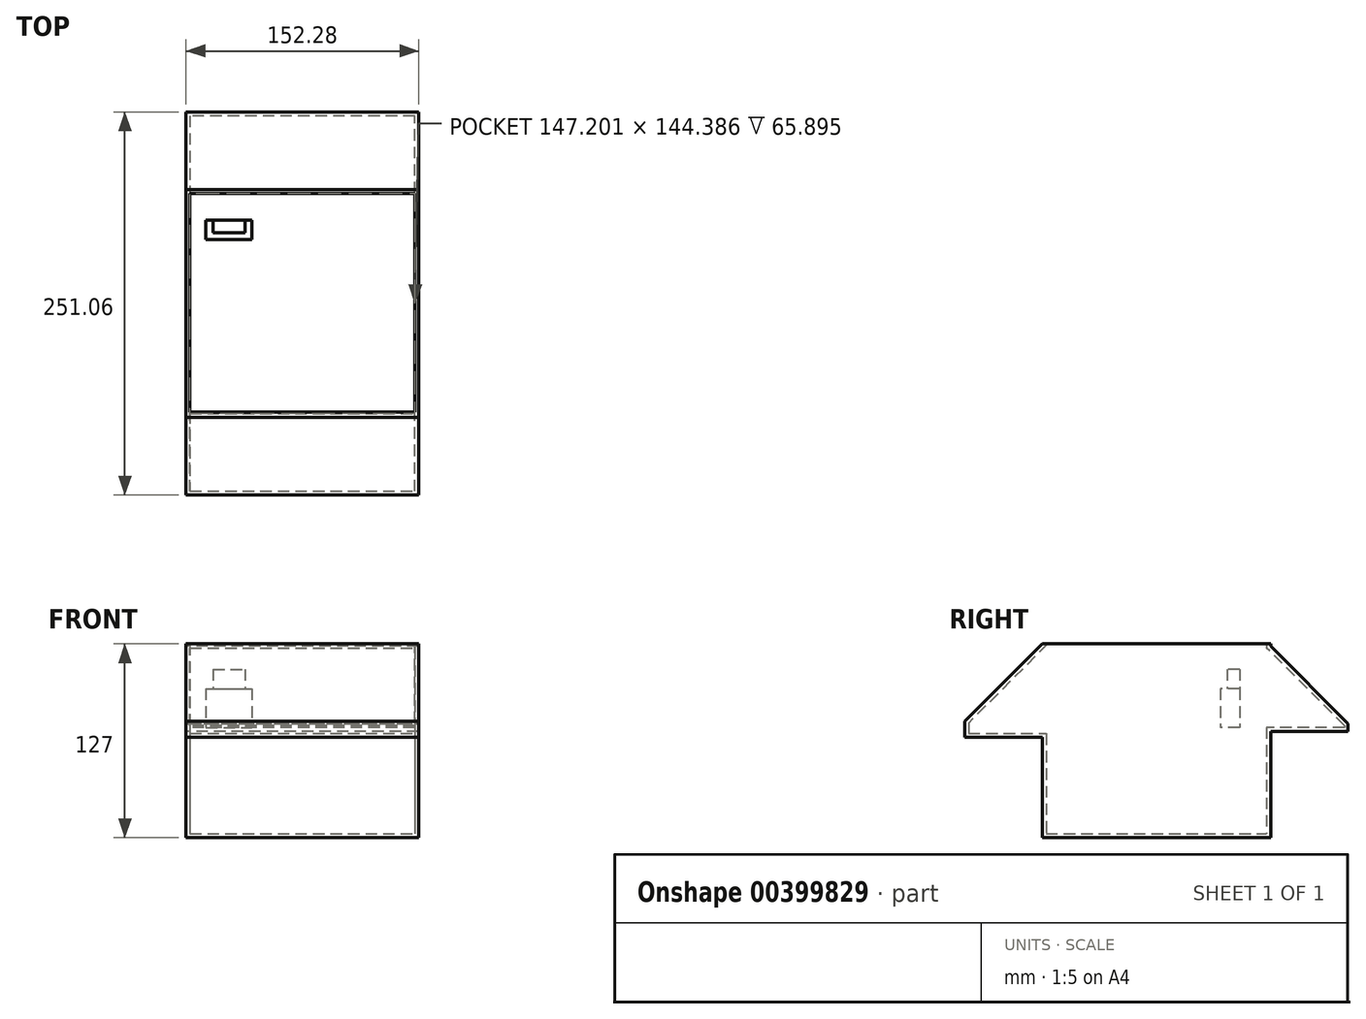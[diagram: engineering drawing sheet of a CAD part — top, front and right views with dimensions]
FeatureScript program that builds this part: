
annotation { "Feature Type Name" : "Feature", "Feature Type Description" : "" }
export const myFeature = defineFeature(function(context is Context, id is Id, definition is map)
    precondition{}
    {
        {
            var Q0;
            Q0=qCreatedBy(makeId("Top.planeOp"),FACE);
            var sketch = newSketch(context, id + "F0", { "sketchPlane" : qUnion([Q0])});
            skLineSegment(sketch, "E0.bottom", {"start": v(-76.8, -74.45) * mm, "end": v(75.48, -74.45) * mm});
            skLineSegment(sketch, "E0.top", {"start": v(-76.8, 75.01) * mm, "end": v(75.48, 75.01) * mm});
            skLineSegment(sketch, "E0.left", {"start": v(-76.8, -74.45) * mm, "end": v(-76.8, 75.01) * mm});
            skLineSegment(sketch, "E0.right", {"start": v(75.48, -74.45) * mm, "end": v(75.48, 75.01) * mm});
            skSolve(sketch);
        }
        {
            var Q0;
            Q0=makeQuery(id+"F0.imprint","IMPRINT",FACE,{"disambiguationData":[TD([[makeQuery(id+"F0.imprint","IMPRINT",EDGE,{"derivedFrom":sQuery(id+"F0.wireOp",EDGE,"E0.bottom")}),1.0]])]});
            extrude(context, id + "F1", {"entities" : qUnion([Q0]), "depth" : 127 * mm});
        }
        {
            var Q0;
            Q0=makeQuery(id+"F1.opExtrude","SWEPT_FACE",FACE,{"disambiguationData":[OSD([sQuery(id+"F0.wireOp",EDGE,"E0.bottom")])]});
            var sketch = newSketch(context, id + "F2", { "sketchPlane" : qUnion([Q0])});
            skLineSegment(sketch, "E1.bottom", {"start": v(-76.8, 127) * mm, "end": v(75.48, 127) * mm});
            skLineSegment(sketch, "E1.top", {"start": v(-76.8, 65.9) * mm, "end": v(75.48, 65.9) * mm});
            skLineSegment(sketch, "E1.left", {"start": v(-76.8, 127) * mm, "end": v(-76.8, 65.9) * mm});
            skLineSegment(sketch, "E1.right", {"start": v(75.48, 127) * mm, "end": v(75.48, 65.9) * mm});
            skSolve(sketch);
        }
        {
            var Q0;
            Q0=makeQuery(id+"F2.imprint","IMPRINT",FACE,{"disambiguationData":[TD([[makeQuery(id+"F2.imprint","IMPRINT",EDGE,{"derivedFrom":sQuery(id+"F2.wireOp",EDGE,"E1.bottom")}),-1.0]])]});
            extrude(context, id + "F3", {"entities" : qUnion([Q0]), "operationType" : NewBodyOperationType.ADD, "depth" : 50.8 * mm});
        }
        {
            var Q0;
            Q0=makeQuery(id+"F1.opExtrude","SWEPT_FACE",FACE,{"disambiguationData":[OSD([sQuery(id+"F0.wireOp",EDGE,"E0.top")])]});
            var sketch = newSketch(context, id + "F4", { "sketchPlane" : qUnion([Q0])});
            skLineSegment(sketch, "E2.bottom", {"start": v(-75.48, 125.47) * mm, "end": v(76.8, 125.47) * mm});
            skLineSegment(sketch, "E2.top", {"start": v(-75.48, 69.75) * mm, "end": v(76.8, 69.75) * mm});
            skLineSegment(sketch, "E2.left", {"start": v(-75.48, 125.47) * mm, "end": v(-75.48, 69.75) * mm});
            skLineSegment(sketch, "E2.right", {"start": v(76.8, 125.47) * mm, "end": v(76.8, 69.75) * mm});
            skSolve(sketch);
        }
        {
            var Q0;
            Q0=makeQuery(id+"F4.imprint","IMPRINT",FACE,{"disambiguationData":[TD([[makeQuery(id+"F4.imprint","IMPRINT",EDGE,{"derivedFrom":sQuery(id+"F4.wireOp",EDGE,"E2.bottom")}),-1.0]])]});
            extrude(context, id + "F5", {"entities" : qUnion([Q0]), "operationType" : NewBodyOperationType.ADD, "depth" : 50.8 * mm});
        }
        {
            var Q0;
            Q0=makeQuery(id+"F5.opExtrude","CAP_EDGE",EDGE,{"disambiguationData":[OSD([sQuery(id+"F4.wireOp",EDGE,"E2.bottom")])],"isStart":false});
            chamfer(context, id + "F6", {"entities" : qUnion([Q0]), "width" : 50.8 * mm, "tangentPropagation" : true});
        }
        {
            var Q0;
            Q0=makeQuery(id+"F3.opExtrude","CAP_EDGE",EDGE,{"disambiguationData":[OSD([sQuery(id+"F2.wireOp",EDGE,"E1.bottom")])],"isStart":false});
            chamfer(context, id + "F7", {"entities" : qUnion([Q0]), "width" : 50.8 * mm, "tangentPropagation" : true});
        }
        {
            var Q0;
            Q0=makeQuery(id+"F3.boolean.opBoolean","MERGE",FACE,{"derivedFrom":[makeQuery(id+"F1.opExtrude","CAP_FACE",FACE,{"disambiguationData":[OSD([sQuery(id+"F0.wireOp",EDGE,"E0.bottom"),sQuery(id+"F0.wireOp",EDGE,"E0.top"),sQuery(id+"F0.wireOp",EDGE,"E0.left"),sQuery(id+"F0.wireOp",EDGE,"E0.right")])],"isStart":false}),makeQuery(id+"F3.opExtrude","SWEPT_FACE",FACE,{"disambiguationData":[OSD([sQuery(id+"F2.wireOp",EDGE,"E1.bottom")])]})]});
            shell(context, id + "F8", {"entities" : qUnion([Q0]), "thickness" : 2.54 * mm});
        }
        {
            var Q0;
            Q0=makeQuery(id+"F8.opShell","OFFSET_FACE",FACE,{"disambiguationData":[OSD([sQuery(id+"F4.wireOp",EDGE,"E2.top")])]});
            var sketch = newSketch(context, id + "F9", { "sketchPlane" : qUnion([Q0])});
            skLineSegment(sketch, "E3.bottom", {"start": v(-63.81, 54.77) * mm, "end": v(-33.88, 54.77) * mm});
            skLineSegment(sketch, "E3.top", {"start": v(-63.81, 42.22) * mm, "end": v(-33.88, 42.22) * mm});
            skLineSegment(sketch, "E3.left", {"start": v(-63.81, 54.77) * mm, "end": v(-63.81, 42.22) * mm});
            skLineSegment(sketch, "E3.right", {"start": v(-33.88, 54.77) * mm, "end": v(-33.88, 42.22) * mm});
            skSolve(sketch);
        }
        {
            var Q0;
            Q0=makeQuery(id+"F9.imprint","IMPRINT",FACE,{"disambiguationData":[TD([[makeQuery(id+"F9.imprint","IMPRINT",EDGE,{"derivedFrom":sQuery(id+"F9.wireOp",EDGE,"E3.bottom")}),-1.0]])]});
            extrude(context, id + "F10", {"entities" : qUnion([Q0]), "depth" : 25.4 * mm});
        }
        {
            var Q0;
            Q0=makeQuery(id+"F10.opExtrude","CAP_FACE",FACE,{"disambiguationData":[OSD([sQuery(id+"F9.wireOp",EDGE,"E3.bottom"),sQuery(id+"F9.wireOp",EDGE,"E3.top"),sQuery(id+"F9.wireOp",EDGE,"E3.left"),sQuery(id+"F9.wireOp",EDGE,"E3.right")])],"isStart":false});
            var sketch = newSketch(context, id + "F11", { "sketchPlane" : qUnion([Q0])});
            skLineSegment(sketch, "E4.bottom", {"start": v(-59.16, 54.77) * mm, "end": v(-38.29, 54.77) * mm});
            skLineSegment(sketch, "E4.top", {"start": v(-59.16, 46.74) * mm, "end": v(-38.29, 46.74) * mm});
            skLineSegment(sketch, "E4.left", {"start": v(-59.16, 54.77) * mm, "end": v(-59.16, 46.74) * mm});
            skLineSegment(sketch, "E4.right", {"start": v(-38.29, 54.77) * mm, "end": v(-38.29, 46.74) * mm});
            skSolve(sketch);
        }
        {
            var Q0;
            Q0=makeQuery(id+"F11.imprint","IMPRINT",FACE,{"disambiguationData":[TD([[makeQuery(id+"F11.imprint","IMPRINT",EDGE,{"derivedFrom":sQuery(id+"F11.wireOp",EDGE,"E4.bottom")}),-1.0]])]});
            extrude(context, id + "F12", {"entities" : qUnion([Q0]), "operationType" : NewBodyOperationType.ADD, "depth" : 12.7 * mm});
        }
    });
